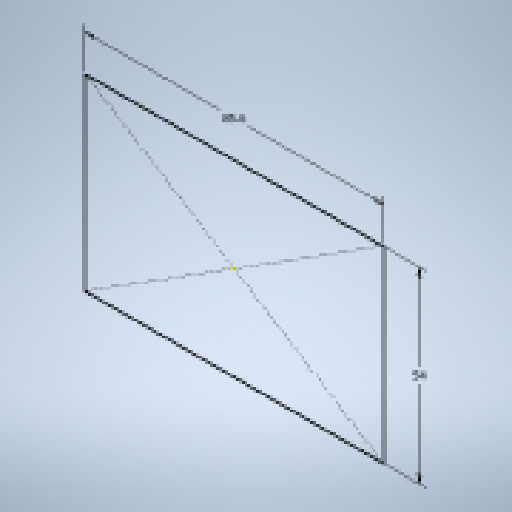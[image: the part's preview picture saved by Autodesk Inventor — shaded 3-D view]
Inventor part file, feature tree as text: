
AUTODESK INVENTOR PART (.ipt)
format: ipt  version: 2023 (Build 270158000, 158)  size: 144,896 bytes
history: native  units: mm
features: other x1, extrude x1, sketch x1
ambient origin geometry x8: Origin, YZ Plane, XZ Plane, XY Plane, X Axis, Y Axis, Z Axis, Center Point
bodies: Body1 (feature_tree)
feature tree (3):
  other  "實體1"
  extrude  "擠出1"  Depth=85.6mm
  sketch  "草圖1"
